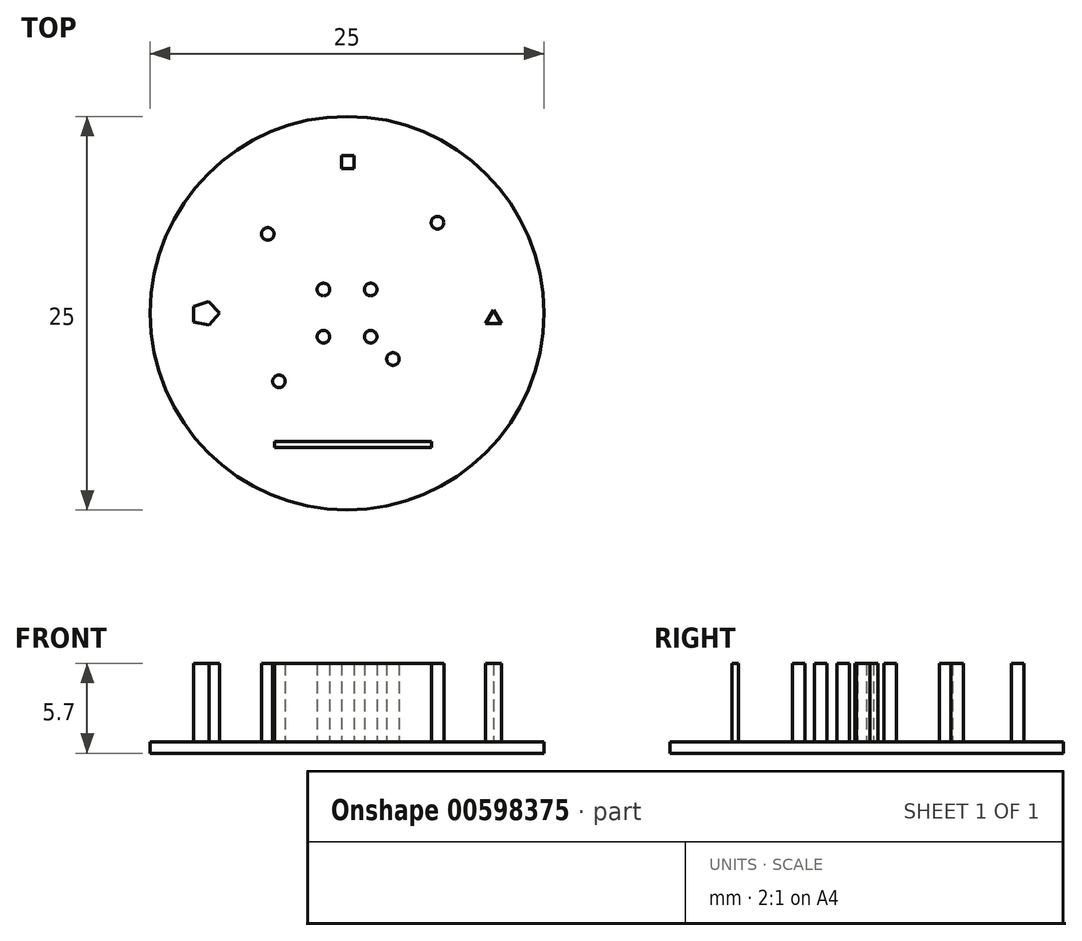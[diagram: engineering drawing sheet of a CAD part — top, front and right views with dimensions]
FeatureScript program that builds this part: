
annotation { "Feature Type Name" : "Feature", "Feature Type Description" : "" }
export const myFeature = defineFeature(function(context is Context, id is Id, definition is map)
    precondition{}
    {
        {
            var Q0;
            Q0=qCreatedBy(makeId("Top.planeOp"),FACE);
            var sketch = newSketch(context, id + "F0", { "sketchPlane" : qUnion([Q0])});
            skCircle(sketch, "E0", {"center": v(0, 0) * mm, "radius": 12.5 * mm});
            skSolve(sketch);
        }
        {
            var Q0;
            Q0=qSketchRegion(id+"F0",true);
            extrude(context, id + "F1", {"entities" : qUnion([Q0]), "depth" : .7 * mm, "offsetDistance" : 25 * mm});
        }
        {
            var Q0;
            Q0=qCreatedBy(makeId("Top.planeOp"),FACE);
            var sketch = newSketch(context, id + "F2", { "sketchPlane" : qUnion([Q0])});
            skCircle(sketch, "E1", {"center": v(-1.5, 1.5) * mm, "radius": 0.4 * mm});
            skCircle(sketch, "E2", {"center": v(-1.5, -1.5) * mm, "radius": 0.4 * mm});
            skCircle(sketch, "E3", {"center": v(1.5, -1.5) * mm, "radius": 0.4 * mm});
            skCircle(sketch, "E4", {"center": v(1.5, 1.5) * mm, "radius": 0.4 * mm});
            skCircle(sketch, "E5", {"center": v(2.91, -2.91) * mm, "radius": 0.4 * mm});
            skCircle(sketch, "E6", {"center": v(5.74, 5.74) * mm, "radius": 0.4 * mm});
            skCircle(sketch, "E7", {"center": v(-5.04, 5.04) * mm, "radius": 0.4 * mm});
            skCircle(sketch, "E8", {"center": v(-4.33, -4.33) * mm, "radius": 0.4 * mm});
            skLineSegment(sketch, "E9.bottom", {"start": v(-0.37, 10) * mm, "end": v(0.43, 10) * mm});
            skLineSegment(sketch, "E9.top", {"start": v(-0.37, 9.2) * mm, "end": v(0.43, 9.2) * mm});
            skLineSegment(sketch, "E9.left", {"start": v(-0.37, 10) * mm, "end": v(-0.37, 9.2) * mm});
            skLineSegment(sketch, "E9.right", {"start": v(0.43, 10) * mm, "end": v(0.43, 9.2) * mm});
            skLineSegment(sketch, "E10", {"start": v(-9.76, 0.43) * mm, "end": v(-9.76, -0.57) * mm});
            skLineSegment(sketch, "E11", {"start": v(-9.76, 0.43) * mm, "end": v(-8.8, 0.72) * mm});
            skLineSegment(sketch, "E12", {"start": v(-9.76, -0.57) * mm, "end": v(-8.77, -0.76) * mm});
            skLineSegment(sketch, "E13", {"start": v(-8.8, 0.72) * mm, "end": v(-8.11, 0) * mm});
            skLineSegment(sketch, "E14", {"start": v(-8.11, 0) * mm, "end": v(-8.77, -0.76) * mm});
            skLineSegment(sketch, "E15", {"start": v(9.3, 0.21) * mm, "end": v(8.8, -0.66) * mm});
            skLineSegment(sketch, "E16", {"start": v(8.8, -0.66) * mm, "end": v(9.8, -0.66) * mm});
            skLineSegment(sketch, "E17", {"start": v(9.8, -0.66) * mm, "end": v(9.3, 0.21) * mm});
            skLineSegment(sketch, "E18.bottom", {"start": v(-4.62, -8.15) * mm, "end": v(5.38, -8.15) * mm});
            skLineSegment(sketch, "E18.top", {"start": v(-4.62, -8.55) * mm, "end": v(5.38, -8.55) * mm});
            skLineSegment(sketch, "E18.left", {"start": v(-4.62, -8.15) * mm, "end": v(-4.62, -8.55) * mm});
            skLineSegment(sketch, "E18.right", {"start": v(5.38, -8.15) * mm, "end": v(5.38, -8.55) * mm});
            skSolve(sketch);
        }
        {
            var Q0;
            Q0=qSketchRegion(id+"F2",true);
            extrude(context, id + "F3", {"entities" : qUnion([Q0]), "operationType" : NewBodyOperationType.ADD, "depth" : 5.7 * mm, "offsetDistance" : 25 * mm});
        }
    });
